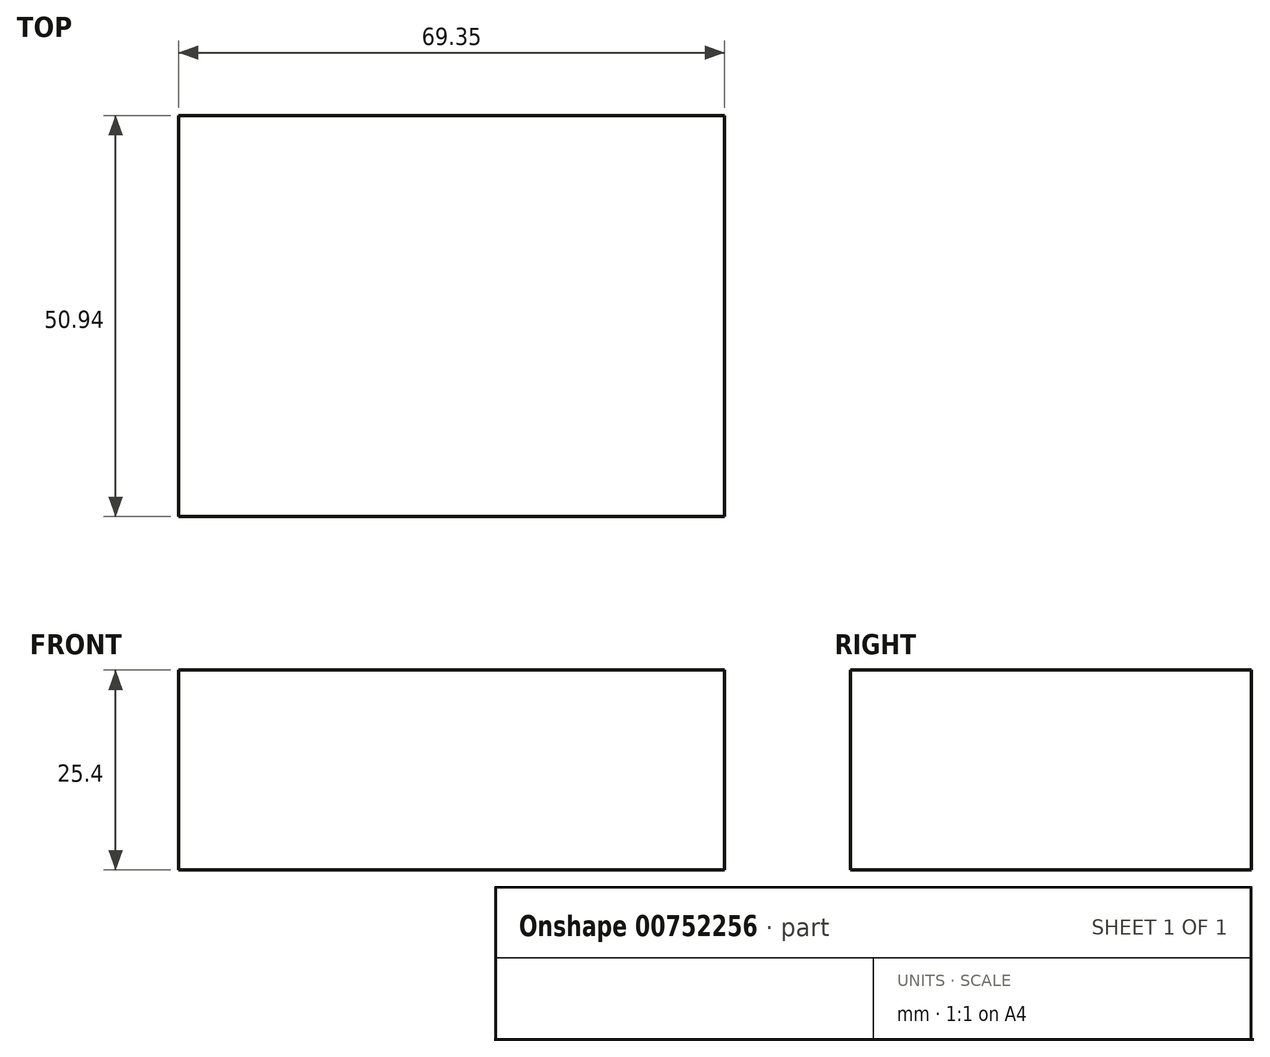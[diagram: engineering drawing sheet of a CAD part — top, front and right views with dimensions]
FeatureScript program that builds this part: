
annotation { "Feature Type Name" : "Feature", "Feature Type Description" : "" }
export const myFeature = defineFeature(function(context is Context, id is Id, definition is map)
    precondition{}
    {
        {
            var Q0;
            Q0=qCreatedBy(makeId("Top.planeOp"),FACE);
            var sketch = newSketch(context, id + "F0", { "sketchPlane" : qUnion([Q0])});
            skLineSegment(sketch, "E0.bottom", {"start": v(-32.9, 32.68) * mm, "end": v(36.45, 32.68) * mm});
            skLineSegment(sketch, "E0.top", {"start": v(-32.9, -18.26) * mm, "end": v(36.45, -18.26) * mm});
            skLineSegment(sketch, "E0.left", {"start": v(-32.9, 32.68) * mm, "end": v(-32.9, -18.26) * mm});
            skLineSegment(sketch, "E0.right", {"start": v(36.45, 32.68) * mm, "end": v(36.45, -18.26) * mm});
            skSolve(sketch);
        }
        {
            var Q0;
            Q0=makeQuery(id+"F0.imprint","IMPRINT",FACE,{"disambiguationData":[TD([[makeQuery(id+"F0.imprint","IMPRINT",EDGE,{"derivedFrom":sQuery(id+"F0.wireOp",EDGE,"E0.bottom")}),-1.0]])]});
            extrude(context, id + "F1", {"entities" : qUnion([Q0]), "endBound" : BoundingType.SYMMETRIC, "depth" : 25.4 * mm, "offsetDistance" : 25.4 * mm});
        }
    });
